# Revit family: WCSeatCover-Duroplast-SoftClosing-Vitra-İstanbulSeries_166
name_source: partatom
category: Plumbing Fixtures
revit_build: Autodesk Revit 2017 (Build: 20160225_1515(x64)
units: mm (PartAtom-declared; Revit-internal decimal feet)

## family parameters
Cut with Voids When Loaded = No
Host = Face
OmniClass Number = 23.45.05.21
OmniClass Title = Plumbing Fixtures - Sanitary Disposal Units
Part Type = Normal
Room Calculation Point = No
Round Connector Dimension = Use Diameter
Shared = Yes

## types (8) — shared parameters
BIMobject category = Sanitary - Toilet Seats
Brand = VitrA
CW Connection = No
Default Elevation = 410 mm  [stored 1.34514 ft]
Description = VitrA İstanbul Slim Wc Seat Model 2 - Round Form Duroplast  Soft-Closing
Design country = Turkey
HW Connection = No
IFC Classification = Sanitary Terminal
Main Material = Duroplast
Manufacturer = Vitra
Manufacturer name = Vitra
NBS Referans Code = 35-93-95
NBS Referans Description = Wc Seats And Covers
Nominal Depth (mm) = 460 mm  [stored 1.50919 ft]
Nominal Height (mm) = 65 mm  [stored 0.213255 ft]
Nominal Width (mm) = 400 mm  [stored 1.31234 ft]
OmniClass Code = 23-31 19 19 11
OmniClass Description = Toilets
Product certification = https://www.vitraglobal.com
Product family = İstanbul
Product group = Toilet Seats
UNSPSC Code = 35-93-95
UNSPSC Description = Water Operated Water Closets
URL = https://www.vitra.com.tr
Uniclass 1.4 Code = L72164
Uniclass 1.4 Description = Toilets
Uniclass 2.0 Code = PR-35-93-95
Uniclass 2.0 Description = Wc Seats And Covers
Uniclass 2015 Code = Pr_40_20_93_95
Uniclass 2015 Name = WC seats and covers
Vent Connection = No
Warranty Period (Year) = 2 Years
Waste Connection = No
Weight Net (kg) = 3.6
Youtube = https://www.youtube.com

## per-type parameters (varying)
| type | Article No. (default) | Color | Model | Primary Material | Product SKU | Product data url | Product url | Technical description |
| WCSeatCover-Duroplast-SoftClosing-Vitra-İstanbulSeries_166-003-109 | 166-003-109 | White | 166-003-109 | White-WCSeat | 166-003-109 | https://www.vitraglobal.com | https://www.vitraglobal.com | https://www.vitraglobal.com |
| WCSeatCover-Duroplast-SoftClosing-Vitra-İstanbulSeries_166-070-109 | 166-070-109 | Black | 166-070-109 | MatteBlack-WCSeat | 166-070-109 | https://www.vitraglobal.com | https://www.vitraglobal.com | https://www.vitraglobal.com |
| WCSeatCover-Duroplast-SoftClosing-MetalHinge-Vitra-İstanbulSeries_166-070-009 | 166-070-009 | Black | 166-070-009 | MatteBlack-WCSeat | 166-070-009 | https://www.vitraglobal.com | https://www.vitraglobal.com | https://www.vitraglobal.com |
| WCSeatCover-Duroplast-SoftClosing-Vitra-İstanbulSeries_166-070H109 | 166-070H109 | Black | 166-070H109 | MatteBlack-WCSeat | 166-070H109 |  | https://www.vitra-india.com | https://www.vitra-india.com |
| WCSeatCover-Duroplast-SoftClosing-Vitra-İstanbulSeries_166-003H109 | 166-003H109 | White | 166-003H109 | White-WCSeat | 166-003H109 |  | https://www.vitra-india.com | https://www.vitra-india.com |
| WCSeatCover-Duroplast-SoftClosing-MetalHinge-Vitra-İstanbulSeries_166-070H009 | 166-070H009 | Black | 166-070H009 | MatteBlack-WCSeat | 166-070H009 |  | https://www.vitra-india.com | https://www.vitra-india.com |
| WCSeatCover-Duroplast-SoftClosing-MetalHinge-Vitra-İstanbulSeries_166-003H009 | 166-003H009 | White | 166-003H009 | White-WCSeat | 166-003H009 |  | https://www.vitra-india.com | https://www.vitra-india.com |
| WCSeatCover-Duroplast-SoftClosing-MetalHinge-Vitra-İstanbulSeries_166-003-009 | 166-003-009 | White | 166-003-009 | White-WCSeat | 166-003-009 |  | https://www.vitra.com.tr | https://www.vitra.com.tr |

note: [stored X ft] marks values corroborated as IEEE doubles in the binary element streams (Revit-internal decimal feet)

## geometry (parser evidence)
native form markers: Sweep x2
no freeform markers — native parametric forms only
